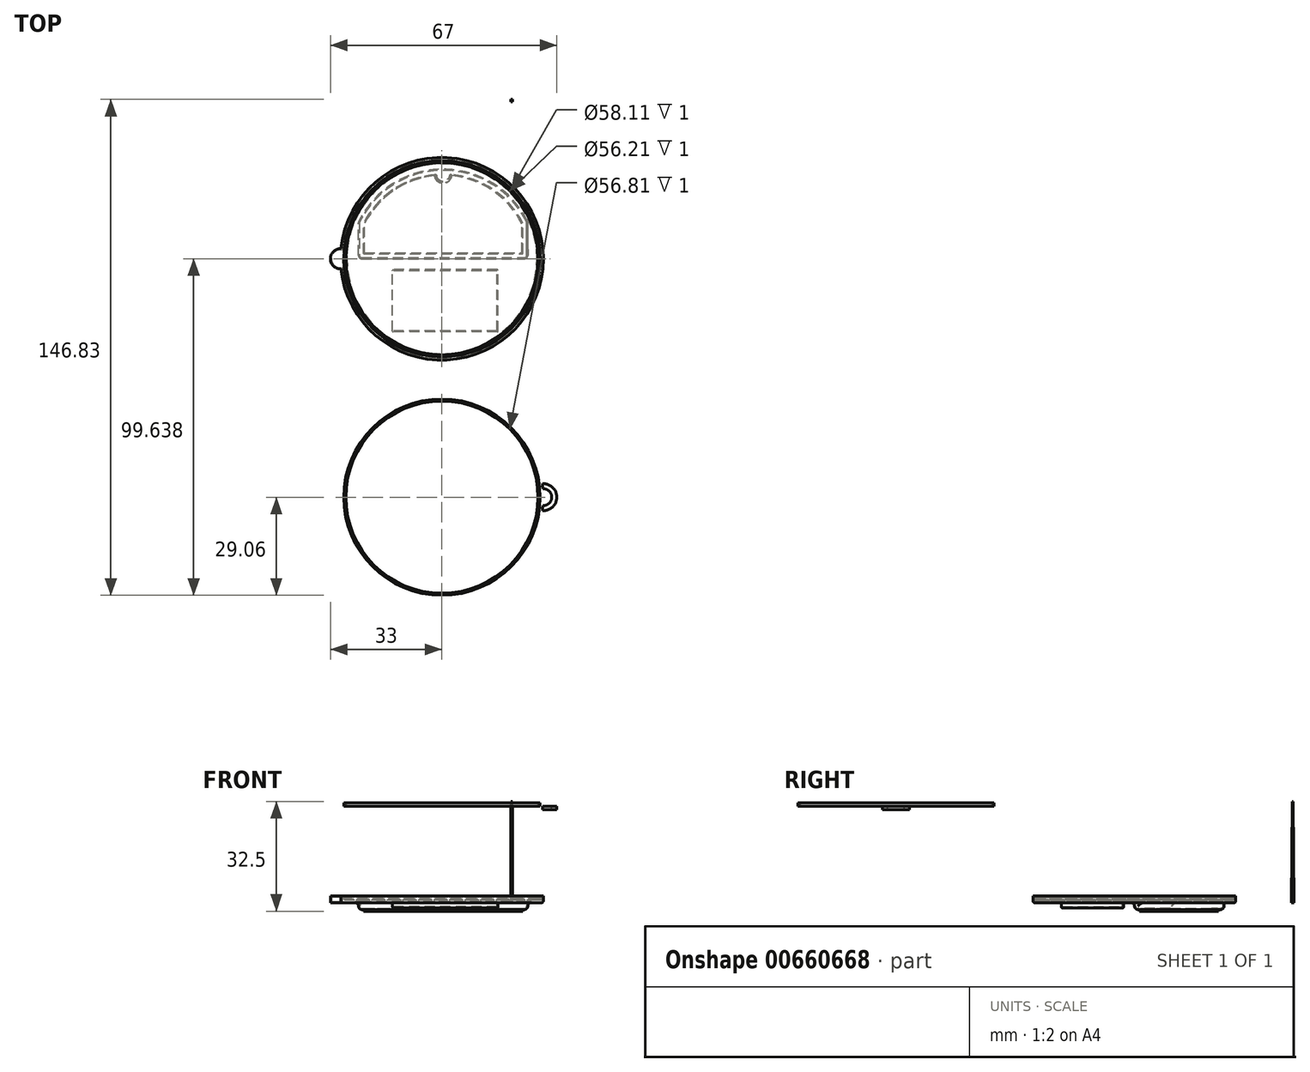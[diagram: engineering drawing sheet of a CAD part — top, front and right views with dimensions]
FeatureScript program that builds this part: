
annotation { "Feature Type Name" : "Feature", "Feature Type Description" : "" }
export const myFeature = defineFeature(function(context is Context, id is Id, definition is map)
    precondition{}
    {
        {
            var Q0;
            Q0=qCreatedBy(makeId("Front.planeOp"),FACE);
            var sketch = newSketch(context, id + "F0", { "sketchPlane" : qUnion([Q0])});
            skLineSegment(sketch, "E0", {"start": v(-28.4, 28.53) * mm, "end": v(-30, 28.53) * mm});
            skLineSegment(sketch, "E1", {"start": v(-30, 28.53) * mm, "end": v(-30, 22.73) * mm});
            skLineSegment(sketch, "E2", {"start": v(-30, 22.73) * mm, "end": v(-28.03, 22.73) * mm});
            skLineSegment(sketch, "E3", {"start": v(-28.03, 22.73) * mm, "end": v(-28.03, 19.85) * mm});
            skLineSegment(sketch, "E4", {"start": v(-28.03, 19.85) * mm, "end": v(-25.46, 19.85) * mm});
            skLineSegment(sketch, "E5", {"start": v(-25.46, 19.85) * mm, "end": v(-25.46, 16.52) * mm});
            skLineSegment(sketch, "E6", {"start": v(-25.46, 16.52) * mm, "end": v(0, 16.52) * mm});
            skLineSegment(sketch, "E7", {"start": v(-28.4, 28.53) * mm, "end": v(-28.4, 24.06) * mm});
            skLineSegment(sketch, "E8", {"start": v(-28.4, 24.06) * mm, "end": v(-26.79, 24.06) * mm});
            skLineSegment(sketch, "E9", {"start": v(-26.79, 24.06) * mm, "end": v(-26.79, 20.82) * mm});
            skLineSegment(sketch, "E10", {"start": v(-26.79, 20.82) * mm, "end": v(-24.35, 20.82) * mm});
            skLineSegment(sketch, "E11", {"start": v(-24.35, 20.82) * mm, "end": v(-24.35, 17.66) * mm});
            skLineSegment(sketch, "E12", {"start": v(-24.35, 17.66) * mm, "end": v(0, 17.66) * mm});
            skPoint(sketch, "E13.orphan", {"position": v(0, 28.53) * mm});
            skLineSegment(sketch, "E14", {"start": v(0, 44.34) * mm, "end": v(0, -10.9) * mm, "construction": true});
            skSolve(sketch);
        }
        {
            var Q0;
            Q0=sQuery(id+"F0.wireOp",EDGE,"E4");
            var Q1;
            Q1=sQuery(id+"F0.wireOp",EDGE,"E7");
            var Q2;
            Q2=sQuery(id+"F0.wireOp",EDGE,"E3");
            var Q3;
            Q3=sQuery(id+"F0.wireOp",EDGE,"E9");
            var Q4;
            Q4=sQuery(id+"F0.wireOp",EDGE,"E5");
            var Q5;
            Q5=sQuery(id+"F0.wireOp",EDGE,"E11");
            var Q6;
            Q6=sQuery(id+"F0.wireOp",EDGE,"E1");
            var Q7;
            Q7=sQuery(id+"F0.wireOp",EDGE,"E8");
            var Q8;
            Q8=sQuery(id+"F0.wireOp",EDGE,"E10");
            var Q9;
            Q9=sQuery(id+"F0.wireOp",EDGE,"E2");
            var Q10;
            Q10=sQuery(id+"F0.wireOp",EDGE,"E0");
            var Q11;
            Q11=sQuery(id+"F0.wireOp",EDGE,"E12");
            var Q12;
            Q12=sQuery(id+"F0.wireOp",EDGE,"E6");
            var Q13;
            Q13=sQuery(id+"F0.wireOp",EDGE,"E14");
            revolve(context, id + "F1", {"bodyType" : ToolBodyType.SURFACE, "surfaceEntities" : qUnion([Q0, Q1, Q2, Q3, Q4, Q5, Q6, Q7, Q8, Q9, Q10, Q11, Q12]), "axis" : qUnion([Q13]), "revolveType" : RevolveType.FULL});
        }
        {
            var Q0;
            Q0=makeQuery(id+"F1.opRevolve","SWEPT_FACE",FACE,{"disambiguationData":[OSD([sQuery(id+"F0.wireOp",EDGE,"E0")])]});
            var sketch = newSketch(context, id + "F2", { "sketchPlane" : qUnion([Q0])});
            skCircle(sketch, "E15.0", {"center": v(0, 0) * mm, "radius": 28.4 * mm});
            skCircle(sketch, "E16", {"center": v(0, 0) * mm, "radius": 29.06 * mm});
            skSolve(sketch);
        }
        {
            var Q0;
            Q0 = qSketchRegion(id + "F2", true);
            extrude(context, id + "F3", {"entities" : qUnion([Q0]), "oppositeDirection" : true, "depth" : 1 * mm, "offsetDistance" : 25 * mm});
        }
        {
            var Q0;
            Q0=qCreatedBy(makeId("Top.planeOp"),FACE);
            var sketch = newSketch(context, id + "F4", { "sketchPlane" : qUnion([Q0])});
            skArc(sketch, "E17", {"start": v(-29.85, 67.58) * mm, "mid": v(30, 70.58) * mm, "end": v(-29.85, 73.57) * mm});
            skArc(sketch, "E18", {"start": v(-29.85, 73.57) * mm, "mid": v(-33, 70.58) * mm, "end": v(-29.85, 67.58) * mm});
            skSolve(sketch);
        }
        {
            var Q0;
            Q0=makeQuery(id+"F4.imprint","IMPRINT",FACE,{"disambiguationData":[TD([[makeQuery(id+"F4.imprint","IMPRINT",EDGE,{"derivedFrom":sQuery(id+"F4.wireOp",EDGE,"E17")}),1.0]])]});
            extrude(context, id + "F5", {"entities" : qUnion([Q0]), "depth" : 2 * mm, "offsetDistance" : 25 * mm});
        }
        {
            var Q0;
            Q0=makeQuery(id+"F5.opExtrude","CAP_FACE",FACE,{"disambiguationData":[OSD([sQuery(id+"F4.wireOp",EDGE,"E17"),sQuery(id+"F4.wireOp",EDGE,"E18")])],"isStart":false});
            var sketch = newSketch(context, id + "F6", { "sketchPlane" : qUnion([Q0])});
            skCircle(sketch, "E19", {"center": v(0, 70.58) * mm, "radius": 28.4 * mm});
            skCircle(sketch, "E20", {"center": v(0, 70.58) * mm, "radius": 29.06 * mm});
            skSolve(sketch);
        }
        {
            var Q0;
            Q0=makeQuery(id+"F6.imprint","IMPRINT",FACE,{"disambiguationData":[TD([[makeQuery(id+"F6.imprint","IMPRINT",EDGE,{"derivedFrom":sQuery(id+"F6.wireOp",EDGE,"E19")}),-1.0]])]});
            extrude(context, id + "F7", {"entities" : qUnion([Q0]), "operationType" : NewBodyOperationType.REMOVE, "oppositeDirection" : true, "depth" : 1 * mm, "offsetDistance" : 25 * mm});
        }
        {
            var Q0;
            Q0=makeQuery(id+"F1.opRevolve","SWEPT_FACE",FACE,{"disambiguationData":[OSD([sQuery(id+"F0.wireOp",EDGE,"E0")])]});
            var sketch = newSketch(context, id + "F8", { "sketchPlane" : qUnion([Q0])});
            skArc(sketch, "E21.0", {"start": v(29.73, -4) * mm, "mid": v(29.82, -3.25) * mm, "end": v(29.9, -2.5) * mm});
            skArc(sketch, "E22", {"start": v(29.73, -4) * mm, "mid": v(34, 0) * mm, "end": v(29.73, 4) * mm});
            skLineSegment(sketch, "E23", {"start": v(0, -37.44) * mm, "end": v(0, 45.75) * mm, "construction": true});
            skArc(sketch, "E24.MirrorC", {"start": v(-29.73, -4) * mm, "mid": v(-34, 0) * mm, "end": v(-29.73, 4) * mm});
            skArc(sketch, "E25.trimOffspring", {"start": v(-29.73, 4) * mm, "mid": v(-29.82, 3.25) * mm, "end": v(-29.9, 2.5) * mm});
            skArc(sketch, "E26", {"start": v(-29.9, 2.5) * mm, "mid": v(-32.5, 0) * mm, "end": v(-29.9, -2.5) * mm});
            skArc(sketch, "E27.MirrorC", {"start": v(29.9, 2.5) * mm, "mid": v(32.5, 0) * mm, "end": v(29.9, -2.5) * mm});
            skArc(sketch, "E28.trimOffspring", {"start": v(-29.9, -2.5) * mm, "mid": v(-29.82, -3.25) * mm, "end": v(-29.73, -4) * mm});
            skArc(sketch, "E29.trimOffspring", {"start": v(29.9, 2.5) * mm, "mid": v(29.82, 3.25) * mm, "end": v(29.73, 4) * mm});
            skSolve(sketch);
        }
        {
            var Q0;
            Q0=makeQuery(id+"F8.imprint","IMPRINT",FACE,{"disambiguationData":[TD([[makeQuery(id+"F8.imprint","IMPRINT",EDGE,{"derivedFrom":sQuery(id+"F8.wireOp",EDGE,"E21.0")}),-1.0]])]});
            var Q1;
            Q1=makeQuery(id+"F8.imprint","IMPRINT",FACE,{"disambiguationData":[TD([[makeQuery(id+"F8.imprint","IMPRINT",EDGE,{"derivedFrom":sQuery(id+"F8.wireOp",EDGE,"E24.MirrorC")}),-1.0]])]});
            extrude(context, id + "F9", {"entities" : qUnion([Q0, Q1]), "depth" : 1 * mm, "offsetDistance" : 25 * mm});
        }
        {
            var Q0;
            Q0=makeQuery(id+"F5.opExtrude","CAP_FACE",FACE,{"disambiguationData":[OSD([sQuery(id+"F4.wireOp",EDGE,"E17"),sQuery(id+"F4.wireOp",EDGE,"E18")])],"isStart":true});
            var sketch = newSketch(context, id + "F10", { "sketchPlane" : qUnion([Q0])});
            skLineSegment(sketch, "E30", {"start": v(-24.7, -70.58) * mm, "end": v(25.44, -70.58) * mm});
            skPoint(sketch, "E30.startSnap0", {"position": v(-33, -70.58) * mm});
            skLineSegment(sketch, "E31", {"start": v(25.44, -70.58) * mm, "end": v(25.44, -81.44) * mm});
            skLineSegment(sketch, "E32", {"start": v(-24.7, -70.58) * mm, "end": v(-24.7, -81.44) * mm});
            skArc(sketch, "E33", {"start": v(-24.7, -81.44) * mm, "mid": v(0.37, -97.08) * mm, "end": v(25.44, -81.44) * mm});
            skPoint(sketch, "E33.first.point", {"position": v(0, -97.08) * mm});
            skSolve(sketch);
        }
        {
            var Q0;
            Q0=makeQuery(id+"F10.imprint","IMPRINT",FACE,{"disambiguationData":[TD([[makeQuery(id+"F10.imprint","IMPRINT",EDGE,{"derivedFrom":sQuery(id+"F10.wireOp",EDGE,"E30")}),-1.0]])]});
            extrude(context, id + "F11", {"entities" : qUnion([Q0]), "operationType" : NewBodyOperationType.ADD, "depth" : 2 * mm, "offsetDistance" : 25 * mm});
        }
        {
            var Q0;
            Q0=makeQuery(id+"F11.opExtrude","CAP_FACE",FACE,{"disambiguationData":[OSD([sQuery(id+"F10.wireOp",EDGE,"E30"),sQuery(id+"F10.wireOp",EDGE,"E31"),sQuery(id+"F10.wireOp",EDGE,"E32"),sQuery(id+"F10.wireOp",EDGE,"E33")])],"isStart":false});
            var sketch = newSketch(context, id + "F12", { "sketchPlane" : qUnion([Q0])});
            skLineSegment(sketch, "E34.0", {"start": v(-23.2, -72.08) * mm, "end": v(-23.2, -81.08) * mm});
            skLineSegment(sketch, "E35.0", {"start": v(-23.2, -72.08) * mm, "end": v(23.94, -72.08) * mm});
            skLineSegment(sketch, "E35.1", {"start": v(23.94, -72.08) * mm, "end": v(23.94, -81.08) * mm});
            skArc(sketch, "E36.0", {"start": v(-23.36, -80.78) * mm, "mid": v(-14.05, -91.3) * mm, "end": v(-0.66, -95.56) * mm});
            skLineSegment(sketch, "E37", {"start": v(0.37, -69.17) * mm, "end": v(0.37, -105.37) * mm, "construction": true});
            skArc(sketch, "E38", {"start": v(1.39, -95.56) * mm, "mid": v(0.37, -94.56) * mm, "end": v(-0.66, -95.56) * mm});
            skArc(sketch, "E39.trimOffspring", {"start": v(1.39, -95.56) * mm, "mid": v(14.78, -91.3) * mm, "end": v(24.1, -80.78) * mm});
            skSolve(sketch);
        }
        {
            var Q0;
            {var subQ1=sQuery(id+"F12.wireOp",EDGE,"E34.0");Q0=makeQuery(id+"F12.imprint","IMPRINT",FACE,{"disambiguationData":[TD([[makeQuery(id+"F12.imprint","IMPRINT",EDGE,{"derivedFrom":subQ1}),1.0]])]});}
            extrude(context, id + "F13", {"entities" : qUnion([Q0]), "operationType" : NewBodyOperationType.ADD, "depth" : 0.5 * mm, "offsetDistance" : 25 * mm});
        }
        {
            var Q0;
            Q0=makeQuery(id+"F11.opExtrude","CAP_EDGE",EDGE,{"disambiguationData":[OSD([sQuery(id+"F10.wireOp",EDGE,"E33")])],"isStart":false});
            var Q1;
            Q1=makeQuery(id+"F11.opExtrude","CAP_EDGE",EDGE,{"disambiguationData":[OSD([sQuery(id+"F10.wireOp",EDGE,"E33")])],"isStart":true});
            var Q2;
            Q2=makeQuery(id+"F11.opExtrude","SWEPT_EDGE",EDGE,{"disambiguationData":[OSD([sQuery(id+"F10.wireOp",EDGE,"E32"),sQuery(id+"F10.wireOp",EDGE,"E33")])]});
            var Q3;
            Q3=makeQuery(id+"F11.opExtrude","SWEPT_EDGE",EDGE,{"disambiguationData":[OSD([sQuery(id+"F10.wireOp",EDGE,"E31"),sQuery(id+"F10.wireOp",EDGE,"E33")])]});
            var Q4;
            Q4=makeQuery(id+"F11.opExtrude","CAP_EDGE",EDGE,{"disambiguationData":[OSD([sQuery(id+"F10.wireOp",EDGE,"E31")])],"isStart":true});
            var Q5;
            Q5=makeQuery(id+"F11.opExtrude","CAP_EDGE",EDGE,{"disambiguationData":[OSD([sQuery(id+"F10.wireOp",EDGE,"E31")])],"isStart":false});
            var Q6;
            Q6=makeQuery(id+"F11.opExtrude","SWEPT_EDGE",EDGE,{"disambiguationData":[OSD([sQuery(id+"F10.wireOp",EDGE,"E30"),sQuery(id+"F10.wireOp",EDGE,"E31")])]});
            var Q7;
            Q7=makeQuery(id+"F11.opExtrude","CAP_EDGE",EDGE,{"disambiguationData":[OSD([sQuery(id+"F10.wireOp",EDGE,"E32")])],"isStart":false});
            var Q8;
            Q8=makeQuery(id+"F11.opExtrude","SWEPT_FACE",FACE,{"disambiguationData":[OSD([sQuery(id+"F10.wireOp",EDGE,"E32")])]});
            var Q9;
            Q9=makeQuery(id+"F11.opExtrude","SWEPT_FACE",FACE,{"disambiguationData":[OSD([sQuery(id+"F10.wireOp",EDGE,"E30")])]});
            fillet(context, id + "F14", {"entities" : qUnion([Q0, Q1, Q2, Q3, Q4, Q5, Q6, Q7, Q8, Q9]), "radius" : 1 * mm, "tangentPropagation" : true, "allowEdgeOverflow" : false});
        }
        {
            var Q0;
            Q0=makeQuery(id+"F13.opExtrude","CAP_EDGE",EDGE,{"disambiguationData":[OSD([sQuery(id+"F12.wireOp",EDGE,"E38")])],"isStart":false});
            chamfer(context, id + "F15", {"entities" : qUnion([Q0]), "width" : 1.5 * mm, "tangentPropagation" : true});
        }
        {
            var Q0;
            Q0=makeQuery(id+"F1.opRevolve","SWEPT_EDGE",EDGE,{"disambiguationData":[OSD([sQuery(id+"F0.wireOp",VERTEX,"E2.start")])]});
            fillet(context, id + "F16", {"entities" : qUnion([Q0]), "radius" : 2 * mm, "tangentPropagation" : true, "allowEdgeOverflow" : false});
        }
        {
            var Q0;
            Q0=makeQuery(id+"F1.opRevolve","SWEPT_EDGE",EDGE,{"disambiguationData":[OSD([sQuery(id+"F0.wireOp",VERTEX,"E3.end")])]});
            fillet(context, id + "F17", {"entities" : qUnion([Q0]), "radius" : 2 * mm, "tangentPropagation" : true, "allowEdgeOverflow" : false});
        }
        {
            var Q0;
            Q0=makeQuery(id+"F1.opRevolve","SWEPT_EDGE",EDGE,{"disambiguationData":[OSD([sQuery(id+"F0.wireOp",VERTEX,"E6.start")])]});
            fillet(context, id + "F18", {"entities" : qUnion([Q0]), "radius" : 2 * mm, "tangentPropagation" : true, "allowEdgeOverflow" : false});
        }
        {
            var Q0;
            Q0=makeQuery(id+"F1.opRevolve","SWEPT_EDGE",EDGE,{"disambiguationData":[OSD([sQuery(id+"F0.wireOp",VERTEX,"E8.start")])]});
            fillet(context, id + "F19", {"entities" : qUnion([Q0]), "radius" : 1 * mm, "tangentPropagation" : true, "allowEdgeOverflow" : false});
        }
        {
            var Q0;
            Q0=makeQuery(id+"F1.opRevolve","SWEPT_EDGE",EDGE,{"disambiguationData":[OSD([sQuery(id+"F0.wireOp",VERTEX,"E8.end")])]});
            fillet(context, id + "F20", {"entities" : qUnion([Q0]), "radius" : 1 * mm, "tangentPropagation" : true, "allowEdgeOverflow" : false});
        }
        {
            var Q0;
            Q0=makeQuery(id+"F1.opRevolve","SWEPT_EDGE",EDGE,{"disambiguationData":[OSD([sQuery(id+"F0.wireOp",VERTEX,"E10.start")])]});
            var Q1;
            Q1=makeQuery(id+"F1.opRevolve","SWEPT_EDGE",EDGE,{"disambiguationData":[OSD([sQuery(id+"F0.wireOp",VERTEX,"E10.end")])]});
            fillet(context, id + "F21", {"entities" : qUnion([Q0, Q1]), "radius" : 1 * mm, "tangentPropagation" : true, "allowEdgeOverflow" : false});
        }
        {
            var Q0;
            Q0=makeQuery(id+"F1.opRevolve","SWEPT_EDGE",EDGE,{"disambiguationData":[OSD([sQuery(id+"F0.wireOp",VERTEX,"E12.start")])]});
            fillet(context, id + "F22", {"entities" : qUnion([Q0]), "radius" : 1 * mm, "tangentPropagation" : true, "allowEdgeOverflow" : false});
        }
        {
            var Q0;
            Q0=makeQuery(id+"F5.opExtrude","CAP_FACE",FACE,{"disambiguationData":[OSD([sQuery(id+"F4.wireOp",EDGE,"E17"),sQuery(id+"F4.wireOp",EDGE,"E18")])],"isStart":true});
            var sketch = newSketch(context, id + "F23", { "sketchPlane" : qUnion([Q0])});
            skLineSegment(sketch, "E40.bottom", {"start": v(16.6, -48.93) * mm, "end": v(-14.6, -48.93) * mm});
            skLineSegment(sketch, "E40.top", {"start": v(16.6, -67.32) * mm, "end": v(-14.6, -67.32) * mm});
            skLineSegment(sketch, "E40.left", {"start": v(16.6, -48.93) * mm, "end": v(16.6, -67.32) * mm});
            skLineSegment(sketch, "E40.right", {"start": v(-14.6, -48.93) * mm, "end": v(-14.6, -67.32) * mm});
            skSolve(sketch);
        }
        {
            var Q0;
            Q0=makeQuery(id+"F23.imprint","IMPRINT",FACE,{"disambiguationData":[TD([[makeQuery(id+"F23.imprint","IMPRINT",EDGE,{"derivedFrom":sQuery(id+"F23.wireOp",EDGE,"E40.bottom")}),1.0]])]});
            extrude(context, id + "F24", {"entities" : qUnion([Q0]), "operationType" : NewBodyOperationType.ADD, "depth" : 1.5 * mm, "offsetDistance" : 25 * mm});
        }
        {
            var Q0;
            Q0=makeQuery(id+"F24.opExtrude","SWEPT_FACE",FACE,{"disambiguationData":[OSD([sQuery(id+"F23.wireOp",EDGE,"E40.right")])]});
            shell(context, id + "F25", {"entities" : qUnion([Q0]), "thickness" : 0.3 * mm});
        }
        {
            var Q0;
            Q0=makeQuery(id+"F24.opExtrude","CAP_EDGE",EDGE,{"disambiguationData":[OSD([sQuery(id+"F23.wireOp",EDGE,"E40.top")])],"isStart":false});
            var Q1;
            Q1=makeQuery(id+"F24.opExtrude","CAP_EDGE",EDGE,{"disambiguationData":[OSD([sQuery(id+"F23.wireOp",EDGE,"E40.top")])],"isStart":true});
            var Q2;
            Q2=makeQuery(id+"F24.opExtrude","CAP_EDGE",EDGE,{"disambiguationData":[OSD([sQuery(id+"F23.wireOp",EDGE,"E40.left")])],"isStart":true});
            var Q3;
            Q3=makeQuery(id+"F24.opExtrude","CAP_EDGE",EDGE,{"disambiguationData":[OSD([sQuery(id+"F23.wireOp",EDGE,"E40.left")])],"isStart":false});
            var Q4;
            Q4=makeQuery(id+"F24.opExtrude","CAP_EDGE",EDGE,{"disambiguationData":[OSD([sQuery(id+"F23.wireOp",EDGE,"E40.bottom")])],"isStart":false});
            var Q5;
            Q5=makeQuery(id+"F24.opExtrude","CAP_EDGE",EDGE,{"disambiguationData":[OSD([sQuery(id+"F23.wireOp",EDGE,"E40.bottom")])],"isStart":true});
            var Q6;
            Q6=makeQuery(id+"F24.opExtrude","CAP_EDGE",EDGE,{"disambiguationData":[OSD([sQuery(id+"F23.wireOp",EDGE,"E40.right")])],"isStart":false});
            var Q7;
            Q7=makeQuery(id+"F24.opExtrude","SWEPT_EDGE",EDGE,{"disambiguationData":[OSD([sQuery(id+"F23.wireOp",EDGE,"E40.bottom"),sQuery(id+"F23.wireOp",EDGE,"E40.right")])]});
            var Q8;
            Q8=makeQuery(id+"F24.opExtrude","SWEPT_EDGE",EDGE,{"disambiguationData":[OSD([sQuery(id+"F23.wireOp",EDGE,"E40.top"),sQuery(id+"F23.wireOp",EDGE,"E40.right")])]});
            var Q9;
            Q9=makeQuery(id+"F24.opExtrude","SWEPT_EDGE",EDGE,{"disambiguationData":[OSD([sQuery(id+"F23.wireOp",EDGE,"E40.top"),sQuery(id+"F23.wireOp",EDGE,"E40.left")])]});
            var Q10;
            Q10=makeQuery(id+"F24.opExtrude","SWEPT_EDGE",EDGE,{"disambiguationData":[OSD([sQuery(id+"F23.wireOp",EDGE,"E40.bottom"),sQuery(id+"F23.wireOp",EDGE,"E40.left")])]});
            fillet(context, id + "F26", {"entities" : qUnion([Q0, Q1, Q2, Q3, Q4, Q5, Q6, Q7, Q8, Q9, Q10]), "radius" : 0.2 * mm, "tangentPropagation" : true, "allowEdgeOverflow" : false});
        }
        {
            var Q0;
            Q0=qCreatedBy(makeId("Top.planeOp"),FACE);
            var sketch = newSketch(context, id + "F27", { "sketchPlane" : qUnion([Q0])});
            skLineSegment(sketch, "E41.bottom", {"start": v(21.67, 116.47) * mm, "end": v(19.64, 116.47) * mm});
            skLineSegment(sketch, "E41.top", {"start": v(21.67, 118.35) * mm, "end": v(19.64, 118.35) * mm});
            skLineSegment(sketch, "E41.left", {"start": v(21.67, 116.47) * mm, "end": v(21.67, 118.35) * mm});
            skLineSegment(sketch, "E41.right", {"start": v(19.64, 116.47) * mm, "end": v(19.64, 118.35) * mm});
            skSolve(sketch);
        }
        {
            var Q0;
            Q0=makeQuery(id+"F27.imprint","IMPRINT",FACE,{"disambiguationData":[TD([[makeQuery(id+"F27.imprint","IMPRINT",EDGE,{"derivedFrom":sQuery(id+"F27.wireOp",EDGE,"E41.bottom")}),-1.0]])]});
            extrude(context, id + "F28", {"entities" : qUnion([Q0]), "depth" : 30 * mm, "offsetDistance" : 25 * mm});
        }
        {
            var Q0;
            Q0=makeQuery(id+"F28.opExtrude","SWEPT_FACE",FACE,{"disambiguationData":[OSD([sQuery(id+"F27.wireOp",EDGE,"E41.right")])]});
            var sketch = newSketch(context, id + "F29", { "sketchPlane" : qUnion([Q0])});
            skLineSegment(sketch, "E42", {"start": v(-117.31, 30) * mm, "end": v(-117.05, 0) * mm});
            skLineSegment(sketch, "E43", {"start": v(-117.51, 30) * mm, "end": v(-117.77, 0) * mm});
            skLineSegment(sketch, "E44", {"start": v(-117.77, 0) * mm, "end": v(-119.65, 0) * mm});
            skLineSegment(sketch, "E45", {"start": v(-119.65, 0) * mm, "end": v(-119.12, 30) * mm});
            skLineSegment(sketch, "E46", {"start": v(-119.12, 30) * mm, "end": v(-117.51, 30) * mm});
            skLineSegment(sketch, "E47", {"start": v(-117.31, 30) * mm, "end": v(-115.6, 30) * mm});
            skLineSegment(sketch, "E48", {"start": v(-115.6, 30) * mm, "end": v(-114.72, 0) * mm});
            skLineSegment(sketch, "E49", {"start": v(-114.72, 0) * mm, "end": v(-117.05, 0) * mm});
            skSolve(sketch);
        }
        {
            var Q0;
            Q0 = qSketchRegion(id + "F29", true);
            extrude(context, id + "F30", {"entities" : qUnion([Q0]), "operationType" : NewBodyOperationType.REMOVE, "oppositeDirection" : true, "depth" : 5 * mm, "offsetDistance" : 25 * mm});
        }
        {
            var Q0;
            Q0=makeQuery(id+"F28.opExtrude","CAP_FACE",FACE,{"disambiguationData":[OSD([sQuery(id+"F27.wireOp",EDGE,"E41.bottom"),sQuery(id+"F27.wireOp",EDGE,"E41.top"),sQuery(id+"F27.wireOp",EDGE,"E41.left"),sQuery(id+"F27.wireOp",EDGE,"E41.right")])],"isStart":true});
            var sketch = newSketch(context, id + "F31", { "sketchPlane" : qUnion([Q0])});
            skLineSegment(sketch, "E50.bottom", {"start": v(21.85, -116.6) * mm, "end": v(20.85, -116.6) * mm});
            skLineSegment(sketch, "E50.top", {"start": v(21.85, -118.22) * mm, "end": v(20.85, -118.22) * mm});
            skLineSegment(sketch, "E50.left", {"start": v(21.85, -116.6) * mm, "end": v(21.85, -118.22) * mm});
            skLineSegment(sketch, "E50.right", {"start": v(20.85, -116.6) * mm, "end": v(20.85, -118.22) * mm});
            skLineSegment(sketch, "E51.bottom", {"start": v(20.45, -116.48) * mm, "end": v(19.38, -116.48) * mm});
            skLineSegment(sketch, "E51.top", {"start": v(20.45, -118.83) * mm, "end": v(19.38, -118.83) * mm});
            skLineSegment(sketch, "E51.left", {"start": v(20.45, -116.48) * mm, "end": v(20.45, -118.83) * mm});
            skLineSegment(sketch, "E51.right", {"start": v(19.38, -116.48) * mm, "end": v(19.38, -118.83) * mm});
            skLineSegment(sketch, "E52", {"start": v(20.65, -117.05) * mm, "end": v(20.65, -119.4) * mm, "construction": true});
            skSolve(sketch);
        }
        {
            var Q0;
            Q0 = qSketchRegion(id + "F31", true);
            extrude(context, id + "F32", {"entities" : qUnion([Q0]), "operationType" : NewBodyOperationType.REMOVE, "oppositeDirection" : true, "depth" : 33.76 * mm, "offsetDistance" : 25 * mm});
        }
        {
            var Q0;
            Q0=makeQuery(id+"F5.opExtrude","CAP_EDGE",EDGE,{"disambiguationData":[OSD([sQuery(id+"F4.wireOp",EDGE,"E17")])],"isStart":true});
            fillet(context, id + "F33", {"entities" : qUnion([Q0]), "radius" : 0.5 * mm, "tangentPropagation" : true, "allowEdgeOverflow" : false});
        }
    });
